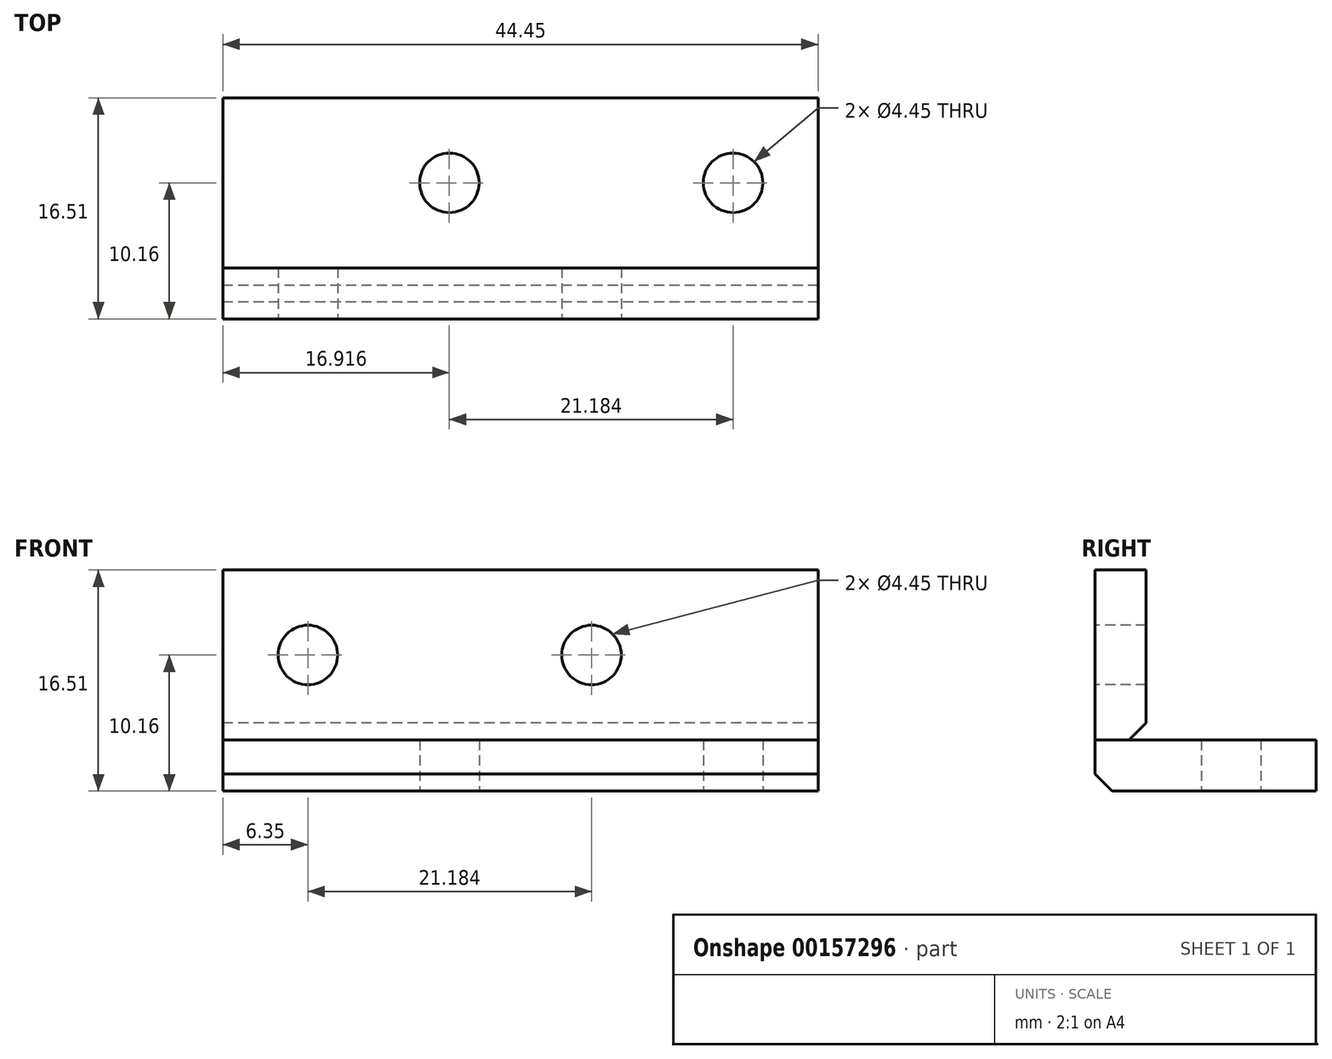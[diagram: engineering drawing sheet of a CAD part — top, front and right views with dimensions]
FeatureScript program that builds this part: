
annotation { "Feature Type Name" : "Feature", "Feature Type Description" : "" }
export const myFeature = defineFeature(function(context is Context, id is Id, definition is map)
    precondition{}
    {
        {
            var Q0;
            Q0=qCreatedBy(makeId("Top.planeOp"),FACE);
            var sketch = newSketch(context, id + "F0", { "sketchPlane" : qUnion([Q0])});
            skLineSegment(sketch, "E0.bottom", {"start": v(0, 0) * mm, "end": v(44.45, 0) * mm});
            skLineSegment(sketch, "E0.top", {"start": v(0, 16.51) * mm, "end": v(44.45, 16.51) * mm});
            skLineSegment(sketch, "E0.left", {"start": v(0, 0) * mm, "end": v(0, 16.51) * mm});
            skLineSegment(sketch, "E0.right", {"start": v(44.45, 0) * mm, "end": v(44.45, 16.51) * mm});
            skCircle(sketch, "E1", {"center": v(38.1, 10.16) * mm, "radius": 2.22 * mm});
            skCircle(sketch, "E2", {"center": v(16.92, 10.16) * mm, "radius": 2.22 * mm});
            skSolve(sketch);
        }
        {
            var Q0;
            Q0=qSketchRegion(id+"F0",true);
            extrude(context, id + "F1", {"entities" : qUnion([Q0]), "depth" : 3.8 * mm});
        }
        {
            var Q0;
            Q0=makeQuery(id+"F1.opExtrude","SWEPT_FACE",FACE,{"disambiguationData":[OSD([sQuery(id+"F0.wireOp",EDGE,"E0.bottom")])]});
            var sketch = newSketch(context, id + "F2", { "sketchPlane" : qUnion([Q0])});
            skCircle(sketch, "E3", {"center": v(6.35, 10.16) * mm, "radius": 2.22 * mm});
            skLineSegment(sketch, "E4.bottom", {"start": v(44.45, 3.81) * mm, "end": v(0, 3.8) * mm});
            skLineSegment(sketch, "E4.top", {"start": v(44.45, 16.51) * mm, "end": v(0, 16.51) * mm});
            skLineSegment(sketch, "E4.left", {"start": v(44.45, 3.81) * mm, "end": v(44.45, 16.51) * mm});
            skLineSegment(sketch, "E4.right", {"start": v(0, 3.81) * mm, "end": v(0, 16.51) * mm});
            skCircle(sketch, "E5", {"center": v(27.53, 10.16) * mm, "radius": 2.22 * mm});
            skSolve(sketch);
        }
        {
            var Q0;
            Q0=qSketchRegion(id+"F2",true);
            extrude(context, id + "F3", {"entities" : qUnion([Q0]), "oppositeDirection" : true, "depth" : 3.8 * mm});
        }
        {
            var Q0;
            Q0=makeQuery(id+"F1.opExtrude","CAP_EDGE",EDGE,{"disambiguationData":[OSD([sQuery(id+"F0.wireOp",EDGE,"E0.bottom")])],"isStart":true});
            chamfer(context, id + "F4", {"entities" : qUnion([Q0]), "width" : 1.27 * mm, "tangentPropagation" : true});
        }
        {
            var Q0;
            Q0=makeQuery(id+"F3.opExtrude","CAP_EDGE",EDGE,{"disambiguationData":[OSD([sQuery(id+"F2.wireOp",EDGE,"E4.bottom")])],"isStart":false});
            chamfer(context, id + "F5", {"entities" : qUnion([Q0]), "width" : 1.27 * mm, "tangentPropagation" : true});
        }
    });
